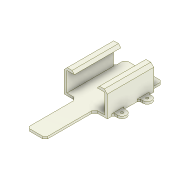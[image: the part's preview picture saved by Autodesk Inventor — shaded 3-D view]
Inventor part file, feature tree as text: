
AUTODESK INVENTOR PART (.ipt)
format: ipt  version: 2022 (Build 260153000, 153)  size: 242,176 bytes
history: native  units: mm
features: chamfer x3, extrude x2, thicken_offset x2, sketch x2, hole x1, mirror x1, projected_geometry x1
ambient origin geometry x8: Origin, YZ Plane, XZ Plane, XY Plane, X Axis, Y Axis, Z Axis, Center Point
bodies: Solid1 (feature_tree)
feature tree (12):
  extrude  "Extrusion1"  Depth=34.0mm
  hole  "Hole1"  [1 undecoded]
  extrude  "Extrusion3"  Depth=6.0mm
  mirror  "Mirror1"
  chamfer  "Chamfer2"  Distance=3.0mm
  chamfer  "Chamfer3"  Distance=2.0mm Angle=45.0deg
  chamfer  "Chamfer4"  Distance=3.0mm Angle=45.0deg
  thicken_offset  "Thicken5"
  thicken_offset  "Thicken6"
  sketch  "Sketch2"  dims[d0=34.0mm d1=69.0mm]
  sketch  "Sketch7"  dims[d2=50.0mm d3=10.0mm d4=6.0mm d5=3.0mm d6=0.0mm d7=3.4mm d8=6.0mm d9=4.0mm d10=2.0mm d11=90.0deg d12=6.0mm d13=0.0mm d29=2.0mm d30=2.0mm d31=45.0deg d32=3.0mm d33=2.0mm d34=45.0deg d35=4.0mm d36=2.0mm d37=45.0deg d52=24.0mm d53=50.0mm d55=145.0mm d56=4.0mm d57=26.0mm d58=4.0mm d59=4.0mm d60=10.0mm d61=3.5mm d62=62.64mm d63=0.0mm d64=0.5mm d65=0.5mm d66=0.5mm d67=0.5mm d68=15.5mm]
  projected_geometry  "Projected Loop1"
note: 1 required parameter value undecoded (feature->parameter linkage not recoverable at this tier; creation-order binding heuristic only, values carry confidence <= 0.55)
